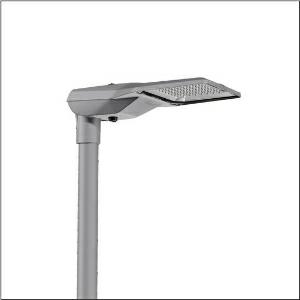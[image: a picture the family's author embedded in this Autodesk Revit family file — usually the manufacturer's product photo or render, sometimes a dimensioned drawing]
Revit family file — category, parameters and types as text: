
# Revit family: streetlight_sl_21_midi___st1_0a_5xe3d33t08nb_d416
name_source: partatom
category: Lighting Fixtures
units: mm (PartAtom-declared; Revit-internal decimal feet)

## family parameters
Cut with Voids When Loaded = No
Host = Face
Light Source = No
Part Type = Normal
Room Calculation Point = No
Round Connector Dimension = Use Diameter
Shared = No

## types (1)
- --- (1 x LED, 22700 lm, 151.2 W, 3000K)
    Apparent Load = 151 VA
    CIE Flux Codes = 40 73 97 100 100
    Color Rendering = 70
    Color Temperature = 3000K
    Default Elevation = 1800 mm
    Description = Streetlight SL 21 midi, mast luminaire, primary light control with lens, of PMMA, primary optical cover: cover, of toughened safety glass, transparent, light distribution: ST1.0a, light emission: direct distribution, primary light characteristic: asymmetric, installation type: side-entry, post-top, LED, High Power LED, rated luminous flux: 22.700lm, luminous efficacy: 150lm/W, light colour: 730, colour temperature: 3000K, control gear: D4i, control: flexible luminous flux parameterisation, time-dependent luminous flux control, constant luminous flux control, overheat protection, pre-setting: logarithmic dimming characteristic, mains connection: 230..240V, AC, 50/60Hz, start of lifetime: 151W, end of service life: 157W, reduction: 70W, luminaire housing, of diecast aluminium, powder-coated, SITECO metallic grey (DB 702S), corrosivity category C5 high according to DIN EN ISO 12944, please order mast flange separately, inclination adjustable: 0°, 5°, 10°, 15°, sealing non-destructively replaceable, multi-level sealing system, length: 644mm, width: 335mm, height: 110mm, mast flange for spigot size: 42mm (side-entry): 5XC10008XM4, 60/48mm (side-entry/post-top): 5XC10108XM2, 76/60mm (side-entry/post-top): 5XC10108XM1, mounting height: 4..8m, Smart Interface below and above, protection rating (complete): IP66, insulation class (complete): insulation class II (safety insulation), certification: CE, ENEC, ENEC+, VDE, impact resistance: IK10, permissible operating ambient temperature for outdoor applications: -40..+50°C, standard-compliant lighting for roads and squares, packaging unit: 1 piece

Light Distribution: ST1.0a
    Height = 111 mm
    Lamp = 1 x LED
    Lamp Light Flux = 22700 lm
    Lamp Power = 151.2 W
    Lamp count = 1
    Length = 644 mm
    Luminous efficacy = 150 lm/W
    Manufacturer = Siteco
    ModVariant = No
    Model = 5XE3D33T08NB
    Number of Poles = 1
    OnlyDefault = Yes
    Power Factor = 1
    Product Name = Streetlight SL 21 midi | ST1.0a
    Product group = mast luminaire | pylon top
    ProductGroupID = 6100
    Protection Class = Protection class II
    Protection Degree = IP 66
    RLX_Detail_Level = 1
    RLX_Emergency_Light_Flux = 0 lm
    RLX_Emergency_Type = 0
    RLX_Emergency_Type_DB = No
    RlxData = <blob elided: 27117 chars, md5=9e8379ab>
    Socket = socket
    Standby Power = 0 W
    System Light Flux = 22700 lm
    System Power = 151 W
    Type Comments = factory setting: luminous flux: 100 % | dim-lin: 254 | 802 mA
    Type Image = l_1004304.jpg
    URL = http://relux.com
    VarID = @adj_169977
    Voltage = 0 V
    Weight = 0.00 kg
    Width = 336 mm

## geometry (parser evidence)
native form markers: Blend x4, Sweep x9
no freeform markers — native parametric forms only
